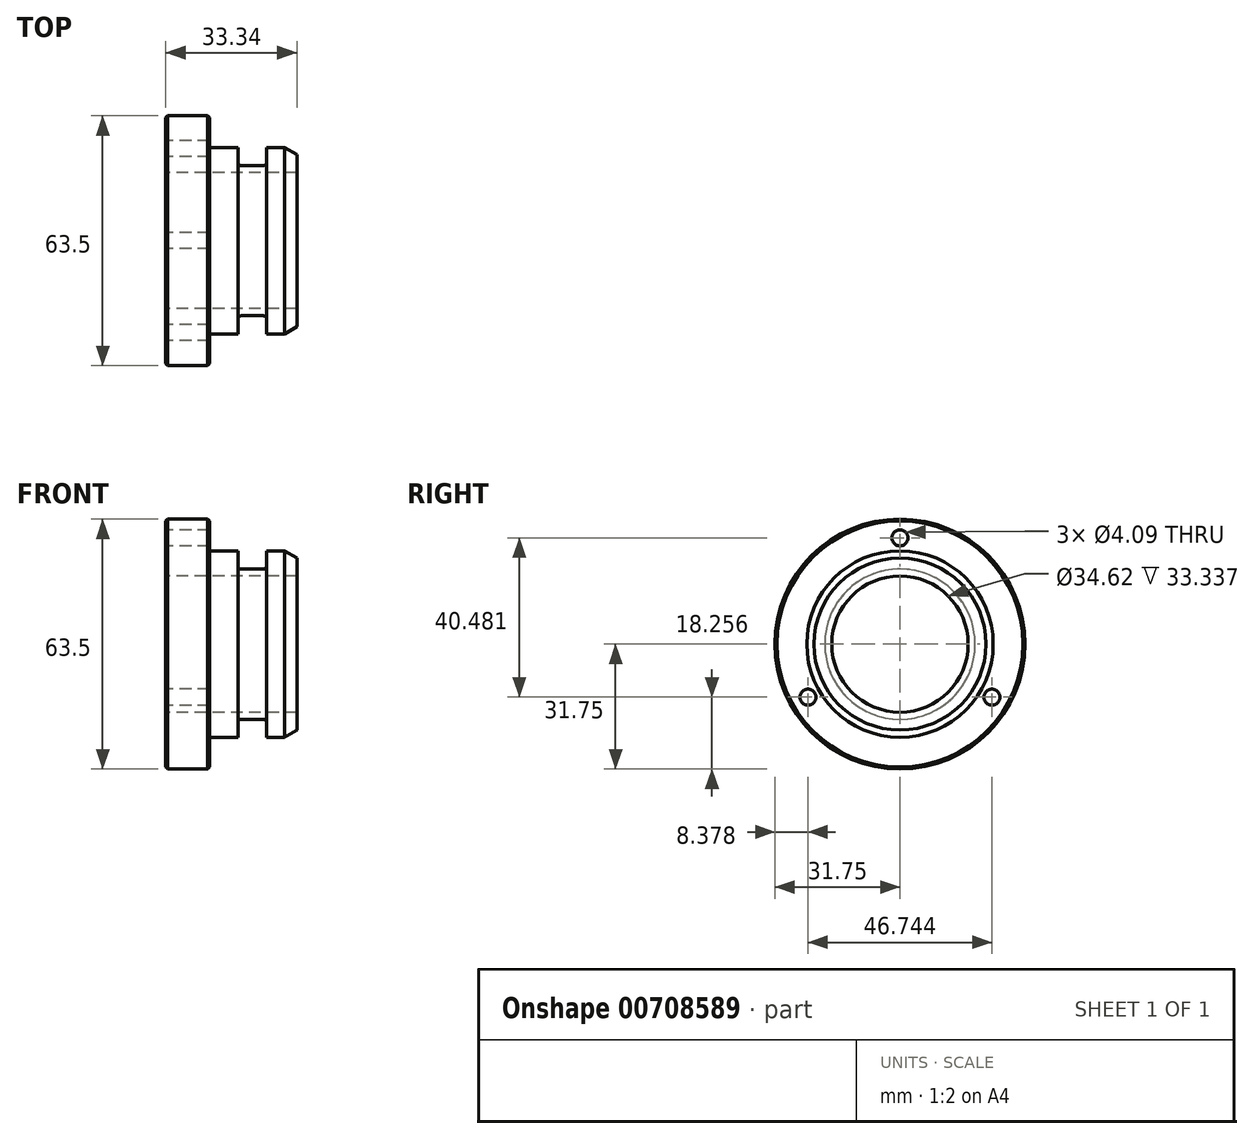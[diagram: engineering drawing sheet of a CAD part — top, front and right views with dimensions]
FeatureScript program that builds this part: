
annotation { "Feature Type Name" : "Feature", "Feature Type Description" : "" }
export const myFeature = defineFeature(function(context is Context, id is Id, definition is map)
    precondition{}
    {
        {
            var Q0;
            Q0=qCreatedBy(makeId("Front.planeOp"),FACE);
            var sketch = newSketch(context, id + "F0", { "sketchPlane" : qUnion([Q0])});
            skLineSegment(sketch, "E0", {"start": v(11.11, 31.75) * mm, "end": v(11.11, 23.68) * mm});
            skLineSegment(sketch, "E1", {"start": v(11.11, 23.68) * mm, "end": v(18.33, 23.68) * mm});
            skLineSegment(sketch, "E2", {"start": v(18.33, 23.68) * mm, "end": v(18.33, 19.1) * mm});
            skLineSegment(sketch, "E3", {"start": v(18.33, 19.1) * mm, "end": v(25.6, 19.1) * mm});
            skLineSegment(sketch, "E4", {"start": v(25.6, 19.1) * mm, "end": v(25.6, 23.68) * mm});
            skLineSegment(sketch, "E5", {"start": v(25.6, 23.68) * mm, "end": v(33.34, 23.68) * mm});
            skLineSegment(sketch, "E6", {"start": v(33.34, 23.68) * mm, "end": v(33.34, 17.31) * mm});
            skLineSegment(sketch, "E7", {"start": v(33.34, 17.31) * mm, "end": v(0, 17.31) * mm});
            skLineSegment(sketch, "E8", {"start": v(11.11, 31.75) * mm, "end": v(0, 31.75) * mm});
            skLineSegment(sketch, "E9", {"start": v(0, 0) * mm, "end": v(47.56, 0) * mm});
            skLineSegment(sketch, "E10", {"start": v(0, 31.75) * mm, "end": v(0, 17.31) * mm});
            skSolve(sketch);
        }
        {
            var Q0;
            Q0=makeQuery(id+"F0.imprint","IMPRINT",FACE,{"disambiguationData":[TD([[makeQuery(id+"F0.imprint","IMPRINT",EDGE,{"derivedFrom":sQuery(id+"F0.wireOp",EDGE,"E0")}),-1.0]])]});
            var Q1;
            Q1=sQuery(id+"F0.wireOp",EDGE,"E9");
            revolve(context, id + "F1", {"surfaceOperationType" : NewSurfaceOperationType.NEW, "entities" : qUnion([Q0]), "axis" : qUnion([Q1]), "revolveType" : RevolveType.FULL});
        }
        {
            var Q0;
            Q0=makeQuery(id+"F1.opRevolve","SWEPT_EDGE",EDGE,{"disambiguationData":[OSD([sQuery(id+"F0.wireOp",EDGE,"E5"),sQuery(id+"F0.wireOp",EDGE,"E6")])]});
            chamfer(context, id + "F2", {"entities" : qUnion([Q0]), "chamferType" : ChamferType.OFFSET_ANGLE, "width" : 3.17 * mm, "oppositeDirection" : false, "angle" : 30 * degree, "tangentPropagation" : true});
        }
        {
            var Q0;
            Q0=makeQuery(id+"F1.opRevolve","SWEPT_EDGE",EDGE,{"disambiguationData":[OSD([sQuery(id+"F0.wireOp",EDGE,"E2"),sQuery(id+"F0.wireOp",EDGE,"E3")])]});
            var Q1;
            Q1=makeQuery(id+"F1.opRevolve","SWEPT_EDGE",EDGE,{"disambiguationData":[OSD([sQuery(id+"F0.wireOp",EDGE,"E3"),sQuery(id+"F0.wireOp",EDGE,"E4")])]});
            fillet(context, id + "F3", {"entities" : qUnion([Q0, Q1]), "radius" : 0.76 * mm, "tangentPropagation" : true, "allowEdgeOverflow" : false});
        }
        {
            var Q0;
            Q0=makeQuery(id+"F1.opRevolve","SWEPT_EDGE",EDGE,{"disambiguationData":[OSD([sQuery(id+"F0.wireOp",EDGE,"E0"),sQuery(id+"F0.wireOp",EDGE,"E1")])]});
            fillet(context, id + "F4", {"entities" : qUnion([Q0]), "radius" : 0.25 * mm, "tangentPropagation" : true, "allowEdgeOverflow" : false});
        }
        {
            var Q0;
            Q0=makeQuery(id+"F1.opRevolve","SWEPT_EDGE",EDGE,{"disambiguationData":[OSD([sQuery(id+"F0.wireOp",EDGE,"E0"),sQuery(id+"F0.wireOp",EDGE,"E8")])]});
            var Q1;
            Q1=makeQuery(id+"F1.opRevolve","SWEPT_EDGE",EDGE,{"disambiguationData":[OSD([sQuery(id+"F0.wireOp",EDGE,"E8"),sQuery(id+"F0.wireOp",EDGE,"E10")])]});
            chamfer(context, id + "F5", {"entities" : qUnion([Q0, Q1]), "width" : 0.5 * mm, "tangentPropagation" : true});
        }
        {
            var Q0;
            Q0=qCreatedBy(makeId("Right.planeOp"),FACE);
            var sketch = newSketch(context, id + "F6", { "sketchPlane" : qUnion([Q0])});
            skCircle(sketch, "E11", {"center": v(0, 26.99) * mm, "radius": 2.04 * mm});
            skCircle(sketch, "E12", {"center": v(23.37, -13.5) * mm, "radius": 2.04 * mm});
            skCircle(sketch, "E13", {"center": v(-23.37, -13.5) * mm, "radius": 2.04 * mm});
            skSolve(sketch);
        }
        {
            var Q0;
            Q0=makeQuery(id+"F6.imprint","IMPRINT",FACE,{"disambiguationData":[TD([[makeQuery(id+"F6.imprint","IMPRINT",EDGE,{"derivedFrom":sQuery(id+"F6.wireOp",EDGE,"E11")}),1.0]])]});
            var Q1;
            Q1=makeQuery(id+"F6.imprint","IMPRINT",FACE,{"disambiguationData":[TD([[makeQuery(id+"F6.imprint","IMPRINT",EDGE,{"derivedFrom":sQuery(id+"F6.wireOp",EDGE,"E12")}),1.0]])]});
            var Q2;
            Q2=makeQuery(id+"F6.imprint","IMPRINT",FACE,{"disambiguationData":[TD([[makeQuery(id+"F6.imprint","IMPRINT",EDGE,{"derivedFrom":sQuery(id+"F6.wireOp",EDGE,"E13")}),1.0]])]});
            var Q3;
            Q3=sQuery(id+"F6.wireOp",EDGE,"E11");
            extrude(context, id + "F7", {"entities" : qUnion([Q0, Q1, Q2]), "operationType" : NewBodyOperationType.REMOVE, "surfaceEntities" : qUnion([Q3]), "depth" : 25.4 * mm, "offsetDistance" : 25.4 * mm});
        }
    });
